# Revit family: Barrier_Gate-Assembly_AutoGate_VPG-NoCrash
name_source: partatom
category: Generic Models
revit_build: Autodesk Revit 2015 (Build: 20140606_1530(x64)
units: mm (PartAtom-declared; Revit-internal decimal feet)

## types (1)
- as Specified
    Assembly Code = E1030900
    Construction Details = http://www.arcat.com
    Default Elevation = 0' - 0"
    Description = AutoGate Vertical Pivot Gate - Gate Design as Specified
    Electrical_Voltage = 24 V
    Expected Lifespan (Years) = 0
    Gate Type = Barrier_Gate_AutoGate_Chainlink-BarbedTop : Size as Specified
    Has Battery Backup = Yes
    Keynote = 32 21 00
    Lift Travel Speed = 10 - 12 seconds
    Maintenance Schedule (Months) = 0
    Manufacturer = AutoGate, Inc
    Manufacturer Fax = 419-588-3514
    Manufacturer Website = http://autogate.com
    Model = Vertical Pivot Gate with Gate Design as Specified
    Product Data = http://www.arcat.com
    Revision = R1_2016-11
    Sales Information = http://autogate.com
    Specification = http://www.arcat.com
    Standards Conformance = UL 325
    Type Comments = Gates over 9' Tall require custom Gate Guard considerations.
    URL = http://autogate.com
    Warranty Duration (Years) = 0
    addwidthA = 0' - 0"
    addwidthB = 0' - 0"

## geometry (parser evidence)
native form markers: Sweep x8
no freeform markers — native parametric forms only
